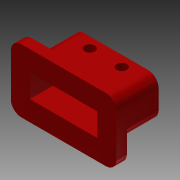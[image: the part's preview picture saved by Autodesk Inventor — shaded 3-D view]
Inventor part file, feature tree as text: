
AUTODESK INVENTOR PART (.ipt)
format: ipt  version: 2015 (Build 190159000, 159)  size: 136,192 bytes
history: native  units: in
note: dims shown in document units (in); Inventor stores cm internally (conversion verified against a paired STEP export)
features: extrude x3, sketch x3, shell x1, fillet x1
ambient origin geometry x8: Origin, YZ Plane, XZ Plane, XY Plane, X Axis, Y Axis, Z Axis, Center Point
bodies: Solid1 (feature_tree)
feature tree (8):
  extrude  "Extrusion1"  Depth=0.474in
  shell  "Shell1"  Thickness=0.5in
  extrude  "Extrusion2"  Depth=0.125in
  extrude  "Extrusion3"  Depth=0.125in
  fillet  "Fillet1"  Radius=0.5in
  sketch  "Sketch1"  dims[d0=1.0in d1=0.474in d2=0.5in d3=0.0in]
  sketch  "Sketch2"  dims[d4=0.1in d23=0.125in]
  sketch  "Sketch3"  dims[d24=0.12in d25=0.38in d26=0.5in d27=0.0in d28=0.75in d29=1.25in d30=0.125in d31=0.125in d32=0.0in d33=0.125in]
